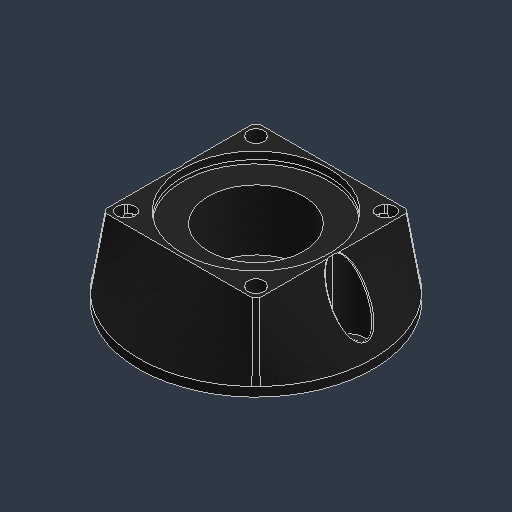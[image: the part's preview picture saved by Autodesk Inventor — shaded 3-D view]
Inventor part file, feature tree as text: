
AUTODESK INVENTOR PART (.ipt)
format: ipt  version: 2024.3 (Build 283343000, 343)  size: 1,020,928 bytes
history: native  units: in
note: dims shown in document units (in); Inventor stores cm internally (conversion verified against a paired STEP export)
features: fillet x1
ambient origin geometry x8: Origin, YZ Plane, XZ Plane, XY Plane, X Axis, Y Axis, Z Axis, Center Point
bodies: Solid1 (feature_tree)
feature tree (1):
  fillet  "Fillet3"  [1 undecoded]
note: 1 required parameter value undecoded (feature->parameter linkage not recoverable at this tier; creation-order binding heuristic only, values carry confidence <= 0.55)
